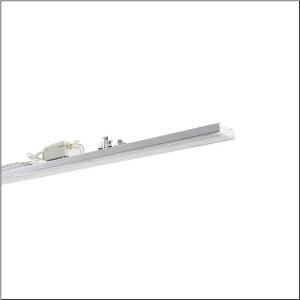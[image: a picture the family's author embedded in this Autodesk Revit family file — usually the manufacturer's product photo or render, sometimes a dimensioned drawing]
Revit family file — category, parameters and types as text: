
# Revit family: licross_21_recessed_mo_52tl11cn49xg
name_source: partatom
category: Lighting Fixtures
units: mm (PartAtom-declared; Revit-internal decimal feet)

## family parameters
Cut with Voids When Loaded = No
Host = Face
Light Source = No
Part Type = Normal
Room Calculation Point = No
Round Connector Dimension = Use Diameter
Shared = No

## types (1)
- --- (1 x LED, 9120 lm, 49.9 W, 4000K)
    Apparent Load = 50 VA
    CIE Flux Codes = 89 96 99 100 100
    Color Rendering = 80
    Color Temperature = 4000K
    Default Elevation = 1800 mm
    Description = Licross 21 Recessed MO, luminaire insert, of sheet steel, galvanised, coil coated, white, length: 1.500mm, width: 66mm, height: 67mm, LED rated luminous flux: 9.120lm, light colour: 840, SDCM (Standard Deviation of Colour Matching)MacAdam ≤ 3 SDCM (initial), control gear: ON/OFF Multilumen, CLOi, with plug, 3-pole, with phase selection, mains connection: 220..240V, AC, 50/60Hz, start of lifetime: 50W, end of service life: 61W, internal wiring halogen-free, primary light control with lens, of plastic, primary optical cover: cover, of PMMA, light emission: direct distribution, primary light characteristic: symmetric, protection rating (complete): IP40, insulation class (complete): insulation class I (protective earthing), certification: CE, ENEC, VDE, UKCA, protection symbol: D if used in an environment without relevant dust loads with corresponding accessories, impact resistance: IK06, permissible ambient temperature for indoor applications: -35..+40°C, corresponds to IFS (International Featured Standards) requirements for safety and quality in the food industry, reducing of maximum allowable ambient temperature of 5°C with ceiling mounting, LABS conformity tested according to VDMA 24364:2018-05, The light source and the operating device comply with the requirements of the Ecodesign Regulation (EU) 2019/2020 and are replaceable in accordance with this regulation, packaging unit: 1 piece
    Height = 58 mm
    Lamp = 1 x LED
    Lamp Light Flux = 9120 lm
    Lamp Power = 49.9 W
    Lamp count = 1
    Length = 1500 mm
    Luminous efficacy = 183 lm/W
    Manufacturer = Siteco
    ModVariant = No
    Model = 52TL11CN49XG
    Mounting Place = Ceiling
    Mounting Type = Pendant
    Number of Poles = 1
    OnlyDefault = Yes
    Power Factor = 1
    Product Name = Licross 21 Recessed MO
    Product group = luminaire insert | ceiling pendant
    ProductGroupID = 901
    Protection Class = Protection class I
    Protection Degree = IP 40
    RLX_Detail_Level = 1
    RLX_Emergency_Light_Flux = 0 lm
    RLX_Emergency_Type = 0
    RLX_Emergency_Type_DB = No
    RlxData = <blob elided: 22525 chars, md5=8c0ddb00>
    Socket = socket
    Standby Power = 0 W
    System Light Flux = 9120 lm
    System Power = 50 W
    Type Comments = factory setting: luminous flux: 100 % | (A | C | E) | 116 mA
    Type Image = l_1296930.jpg
    URL = http://relux.com
    VarID = @adj_112189
    Voltage = 0 V
    Weight = 0.00 kg
    Width = 66 mm

## geometry (parser evidence)
native form markers: Blend x4, Sweep x10
no freeform markers — native parametric forms only
